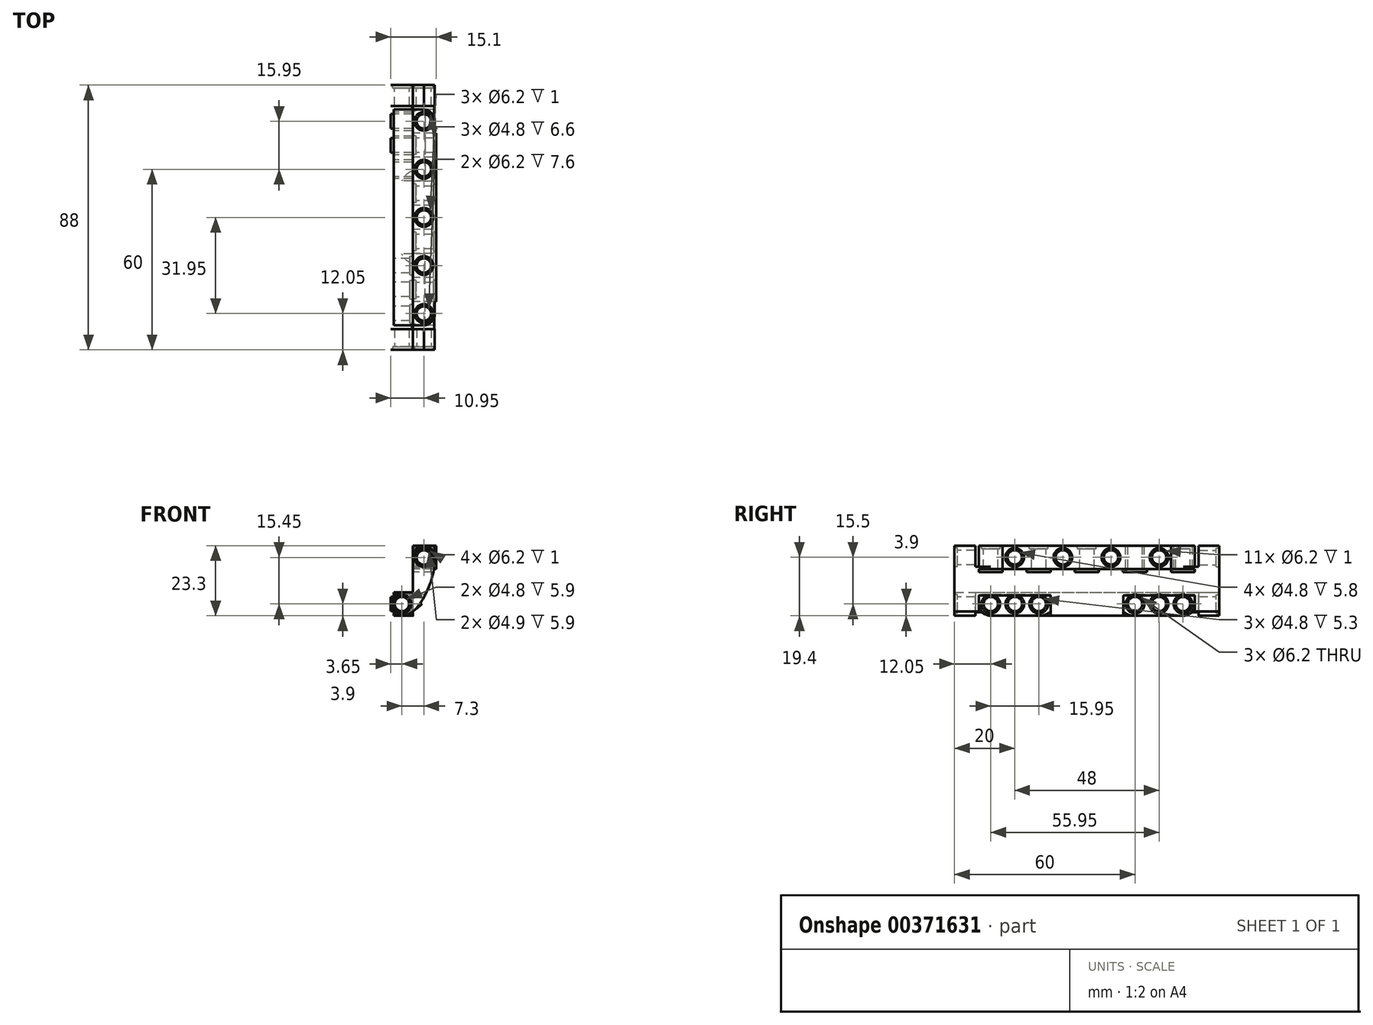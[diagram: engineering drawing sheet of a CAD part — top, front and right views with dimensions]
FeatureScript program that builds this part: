
annotation { "Feature Type Name" : "Feature", "Feature Type Description" : "" }
export const myFeature = defineFeature(function(context is Context, id is Id, definition is map)
    precondition{}
    {
        {
            var Q0;
            Q0=qCreatedBy(makeId("Front.planeOp"),FACE);
            var sketch = newSketch(context, id + "F0", { "sketchPlane" : qUnion([Q0])});
            skLineSegment(sketch, "E0", {"start": v(0, 0) * mm, "end": v(0, -11.65) * mm});
            skLineSegment(sketch, "E1", {"start": v(7.3, -11.65) * mm, "end": v(0, -11.65) * mm});
            skLineSegment(sketch, "E2", {"start": v(0, -11.65) * mm, "end": v(-7.3, -11.65) * mm});
            skLineSegment(sketch, "E3", {"start": v(-7.3, -11.65) * mm, "end": v(-7.3, -3.85) * mm});
            skLineSegment(sketch, "E4", {"start": v(-7.3, -3.85) * mm, "end": v(0, -3.85) * mm});
            skLineSegment(sketch, "E5", {"start": v(0, 0) * mm, "end": v(0, 11.65) * mm});
            skLineSegment(sketch, "E6", {"start": v(0, 11.65) * mm, "end": v(7.3, 11.65) * mm});
            skLineSegment(sketch, "E7", {"start": v(7.3, 11.65) * mm, "end": v(7.3, -11.65) * mm});
            skLineSegment(sketch, "E8", {"start": v(-3.65, -11.65) * mm, "end": v(-3.65, -3.85) * mm, "construction": true});
            skLineSegment(sketch, "E9", {"start": v(-7.3, -7.75) * mm, "end": v(0, -7.75) * mm, "construction": true});
            skLineSegment(sketch, "E10", {"start": v(3.65, 11.65) * mm, "end": v(3.65, -11.65) * mm, "construction": true});
            skLineSegment(sketch, "E11", {"start": v(7.3, 11.65) * mm, "end": v(7.3, 3.75) * mm, "construction": true});
            skLineSegment(sketch, "E12", {"start": v(7.3, 7.7) * mm, "end": v(0, 7.7) * mm, "construction": true});
            skLineSegment(sketch, "E13", {"start": v(0, -3.85) * mm, "end": v(4.5, -3.85) * mm, "construction": true});
            skFitSpline(sketch, "E14", {"points": [v(7.3, 7.7) * mm, v(4.5, -3.85) * mm, v(-3.65, -11.65) * mm], "startDerivative": vector(0, -23.4) * mm, "endDerivative": vector(-22.19, 0) * mm});
            skCircle(sketch, "E15", {"center": v(3.65, 7.7) * mm, "radius": 3.1 * mm});
            skCircle(sketch, "E16", {"center": v(3.65, 7.7) * mm, "radius": 2.45 * mm});
            skCircle(sketch, "E17", {"center": v(-3.65, -7.75) * mm, "radius": 2.45 * mm});
            skCircle(sketch, "E18", {"center": v(-3.65, -7.75) * mm, "radius": 3.1 * mm});
            skSolve(sketch);
        }
        {
            var Q0;
            {var subQ1=sQuery(id+"F0.wireOp",EDGE,"E5");Q0=makeQuery(id+"F0.imprint","IMPRINT",FACE,{"disambiguationData":[TD([[makeQuery(id+"F0.imprint","IMPRINT",EDGE,{"derivedFrom":subQ1}),-1.0]])]});}
            var Q1;
            {var subQ1=sQuery(id+"F0.wireOp",EDGE,"E3");Q1=makeQuery(id+"F0.imprint","IMPRINT",FACE,{"disambiguationData":[TD([[makeQuery(id+"F0.imprint","IMPRINT",EDGE,{"derivedFrom":subQ1}),-1.0]])]});}
            var Q2;
            Q2=makeQuery(id+"F0.imprint","IMPRINT",FACE,{"disambiguationData":[TD([[makeQuery(id+"F0.imprint","IMPRINT",EDGE,{"derivedFrom":sQuery(id+"F0.wireOp",EDGE,"E15")}),1.0]])]});
            var Q3;
            Q3=makeQuery(id+"F0.imprint","IMPRINT",FACE,{"disambiguationData":[TD([[makeQuery(id+"F0.imprint","IMPRINT",EDGE,{"derivedFrom":sQuery(id+"F0.wireOp",EDGE,"E16")}),1.0]])]});
            var Q4;
            Q4=makeQuery(id+"F0.imprint","IMPRINT",FACE,{"disambiguationData":[TD([[makeQuery(id+"F0.imprint","IMPRINT",EDGE,{"derivedFrom":sQuery(id+"F0.wireOp",EDGE,"E17")}),-1.0]])]});
            var Q5;
            Q5=makeQuery(id+"F0.imprint","IMPRINT",FACE,{"disambiguationData":[TD([[makeQuery(id+"F0.imprint","IMPRINT",EDGE,{"derivedFrom":sQuery(id+"F0.wireOp",EDGE,"E17")}),1.0]])]});
            extrude(context, id + "F1", {"entities" : qUnion([Q0, Q1, Q2, Q3, Q4, Q5]), "depth" : 88 * mm});
        }
        {
            var Q0;
            Q0=makeQuery(id+"F0.imprint","IMPRINT",FACE,{"disambiguationData":[TD([[makeQuery(id+"F0.imprint","IMPRINT",EDGE,{"derivedFrom":sQuery(id+"F0.wireOp",EDGE,"E17")}),1.0]])]});
            var Q1;
            Q1=makeQuery(id+"F0.imprint","IMPRINT",FACE,{"disambiguationData":[TD([[makeQuery(id+"F0.imprint","IMPRINT",EDGE,{"derivedFrom":sQuery(id+"F0.wireOp",EDGE,"E16")}),1.0]])]});
            extrude(context, id + "F2", {"entities" : qUnion([Q0, Q1]), "operationType" : NewBodyOperationType.REMOVE, "depth" : 7.8 * mm});
        }
        {
            var Q0;
            Q0=makeQuery(id+"F0.imprint","IMPRINT",FACE,{"disambiguationData":[TD([[makeQuery(id+"F0.imprint","IMPRINT",EDGE,{"derivedFrom":sQuery(id+"F0.wireOp",EDGE,"E17")}),-1.0]])]});
            var Q1;
            Q1=makeQuery(id+"F0.imprint","IMPRINT",FACE,{"disambiguationData":[TD([[makeQuery(id+"F0.imprint","IMPRINT",EDGE,{"derivedFrom":sQuery(id+"F0.wireOp",EDGE,"E15")}),1.0]])]});
            extrude(context, id + "F3", {"entities" : qUnion([Q0, Q1]), "operationType" : NewBodyOperationType.REMOVE, "depth" : 1 * mm});
        }
        {
            var Q0;
            Q0=makeQuery(id+"F1.opExtrude","SWEPT_FACE",FACE,{"disambiguationData":[OSD([sQuery(id+"F0.wireOp",EDGE,"E6")])]});
            var sketch = newSketch(context, id + "F4", { "sketchPlane" : qUnion([Q0])});
            skLineSegment(sketch, "E19", {"start": v(7.3, -44) * mm, "end": v(0, -44) * mm, "construction": true});
            skLineSegment(sketch, "E20", {"start": v(7.3, -44) * mm, "end": v(7.3, -76) * mm});
            skLineSegment(sketch, "E21", {"start": v(0, -44) * mm, "end": v(0, -48) * mm, "construction": true});
            skLineSegment(sketch, "E22", {"start": v(0, -48) * mm, "end": v(7.83, -48) * mm});
            skLineSegment(sketch, "E23", {"start": v(0, -48) * mm, "end": v(0, -56) * mm});
            skLineSegment(sketch, "E24", {"start": v(0, -56) * mm, "end": v(0, -64) * mm});
            skLineSegment(sketch, "E25", {"start": v(0, -64) * mm, "end": v(0, -72) * mm});
            skLineSegment(sketch, "E26", {"start": v(0, -72) * mm, "end": v(0, -76) * mm});
            skLineSegment(sketch, "E27", {"start": v(3.4, -79.9) * mm, "end": v(3.9, -79.9) * mm});
            skLineSegment(sketch, "E28", {"start": v(0, -72) * mm, "end": v(7.8, -72) * mm});
            skLineSegment(sketch, "E29", {"start": v(7.8, -72) * mm, "end": v(7.8, -44) * mm});
            skLineSegment(sketch, "E30", {"start": v(3.65, -79.9) * mm, "end": v(3.65, -44) * mm, "construction": true});
            skLineSegment(sketch, "E31", {"start": v(0, -60) * mm, "end": v(7.3, -60) * mm, "construction": true});
            skLineSegment(sketch, "E32", {"start": v(0, -75.95) * mm, "end": v(7.3, -75.95) * mm, "construction": true});
            skCircle(sketch, "E33", {"center": v(3.65, -75.95) * mm, "radius": 2.4 * mm});
            skCircle(sketch, "E34", {"center": v(3.65, -75.95) * mm, "radius": 3.1 * mm});
            skCircle(sketch, "E35", {"center": v(3.65, -60) * mm, "radius": 2.4 * mm});
            skCircle(sketch, "E36", {"center": v(3.65, -60) * mm, "radius": 3.1 * mm});
            skCircle(sketch, "E37", {"center": v(3.65, -44) * mm, "radius": 2.4 * mm});
            skCircle(sketch, "E38", {"center": v(3.65, -44) * mm, "radius": 3.1 * mm});
            skLineSegment(sketch, "E39.MirrorCS", {"start": v(7.8, -16) * mm, "end": v(7.8, -44) * mm});
            skLineSegment(sketch, "E40.MirrorCS", {"start": v(0, -16) * mm, "end": v(7.8, -16) * mm});
            skCircle(sketch, "E41.MirrorC", {"center": v(3.65, -12.05) * mm, "radius": 2.4 * mm});
            skCircle(sketch, "E42.MirrorC", {"center": v(3.65, -12.05) * mm, "radius": 3.1 * mm});
            skCircle(sketch, "E43.MirrorC", {"center": v(3.65, -28) * mm, "radius": 3.1 * mm});
            skCircle(sketch, "E44.MirrorC", {"center": v(3.65, -28) * mm, "radius": 2.4 * mm});
            skLineSegment(sketch, "E45.MirrorCS", {"start": v(0, -8.1) * mm, "end": v(7.3, -8.1) * mm});
            skLineSegment(sketch, "E46.MirrorCS", {"start": v(7.3, -44) * mm, "end": v(14.6, -44) * mm, "construction": true});
            skLineSegment(sketch, "E47.MirrorCS", {"start": v(7.3, -44) * mm, "end": v(7.3, -8.1) * mm});
            skLineSegment(sketch, "E48.MirrorCS", {"start": v(0, -16) * mm, "end": v(0, -8.1) * mm});
            skPoint(sketch, "E49.visualSharp", {"position": v(7.3, -79.9) * mm});
            skArc(sketch, "E49.filletArc", {"start": v(3.4, -79.9) * mm, "mid": v(6.16, -78.76) * mm, "end": v(7.3, -76) * mm});
            skPoint(sketch, "E50.visualSharp", {"position": v(0, -79.9) * mm});
            skArc(sketch, "E50.filletArc", {"start": v(0, -76) * mm, "mid": v(1.14, -78.76) * mm, "end": v(3.9, -79.9) * mm});
            skArc(sketch, "E51.MirrorCS", {"start": v(3.4, -8.1) * mm, "mid": v(6.16, -9.24) * mm, "end": v(7.3, -12) * mm});
            skArc(sketch, "E52.MirrorCS", {"start": v(0, -12) * mm, "mid": v(1.14, -9.24) * mm, "end": v(3.9, -8.1) * mm});
            skLineSegment(sketch, "E53", {"start": v(7.3, -88) * mm, "end": v(7.3, -81.1) * mm});
            skLineSegment(sketch, "E54", {"start": v(7.3, -81.1) * mm, "end": v(0, -81.1) * mm});
            skLineSegment(sketch, "E55", {"start": v(0, -81.1) * mm, "end": v(0, -79.9) * mm});
            skLineSegment(sketch, "E56", {"start": v(7.3, -79.9) * mm, "end": v(0, -79.9) * mm});
            skLineSegment(sketch, "E57.MirrorCS", {"start": v(7.3, -8.1) * mm, "end": v(0, -8.1) * mm});
            skLineSegment(sketch, "E58.MirrorCS", {"start": v(7.3, -6.9) * mm, "end": v(0, -6.9) * mm});
            skSolve(sketch);
        }
        {
            var Q0;
            {var subQ0=sQuery(id+"F4.wireOp",EDGE,"E58.MirrorCS");Q0=makeQuery(id+"F4.imprint","IMPRINT",FACE,{"disambiguationData":[TD([[makeQuery(id+"F4.imprint","IMPRINT",EDGE,{"derivedFrom":subQ0}),1.0]])]});}
            var Q1;
            {var subQ7=sQuery(id+"F4.wireOp",EDGE,"E54");Q1=makeQuery(id+"F4.imprint","IMPRINT",FACE,{"disambiguationData":[TD([[makeQuery(id+"F4.imprint","IMPRINT",EDGE,{"derivedFrom":subQ7}),-1.0]])]});}
            extrude(context, id + "F5", {"entities" : qUnion([Q0, Q1]), "operationType" : NewBodyOperationType.REMOVE, "oppositeDirection" : true, "depth" : 7 * mm});
        }
        {
            var Q0;
            Q0=makeQuery(id+"F4.imprint","IMPRINT",FACE,{"disambiguationData":[TD([[makeQuery(id+"F4.imprint","IMPRINT",EDGE,{"derivedFrom":sQuery(id+"F4.wireOp",EDGE,"E41.MirrorC")}),-1.0]])]});
            var Q1;
            Q1=makeQuery(id+"F4.imprint","IMPRINT",FACE,{"disambiguationData":[TD([[makeQuery(id+"F4.imprint","IMPRINT",EDGE,{"derivedFrom":sQuery(id+"F4.wireOp",EDGE,"E44.MirrorC")}),-1.0]])]});
            var Q2;
            Q2=makeQuery(id+"F4.imprint","IMPRINT",FACE,{"disambiguationData":[TD([[makeQuery(id+"F4.imprint","IMPRINT",EDGE,{"derivedFrom":sQuery(id+"F4.wireOp",EDGE,"E37")}),1.0]])]});
            var Q3;
            Q3=makeQuery(id+"F4.imprint","IMPRINT",FACE,{"disambiguationData":[TD([[makeQuery(id+"F4.imprint","IMPRINT",EDGE,{"derivedFrom":sQuery(id+"F4.wireOp",EDGE,"E35")}),1.0]])]});
            var Q4;
            Q4=makeQuery(id+"F4.imprint","IMPRINT",FACE,{"disambiguationData":[TD([[makeQuery(id+"F4.imprint","IMPRINT",EDGE,{"derivedFrom":sQuery(id+"F4.wireOp",EDGE,"E33")}),1.0]])]});
            extrude(context, id + "F6", {"entities" : qUnion([Q0, Q1, Q2, Q3, Q4]), "operationType" : NewBodyOperationType.REMOVE, "oppositeDirection" : true, "depth" : 7.6 * mm});
        }
        {
            var Q0;
            Q0=makeQuery(id+"F4.imprint","IMPRINT",FACE,{"disambiguationData":[TD([[makeQuery(id+"F4.imprint","IMPRINT",EDGE,{"derivedFrom":sQuery(id+"F4.wireOp",EDGE,"E41.MirrorC")}),1.0]])]});
            var Q1;
            Q1=makeQuery(id+"F4.imprint","IMPRINT",FACE,{"disambiguationData":[TD([[makeQuery(id+"F4.imprint","IMPRINT",EDGE,{"derivedFrom":sQuery(id+"F4.wireOp",EDGE,"E43.MirrorC")}),-1.0]])]});
            var Q2;
            Q2=makeQuery(id+"F4.imprint","IMPRINT",FACE,{"disambiguationData":[TD([[makeQuery(id+"F4.imprint","IMPRINT",EDGE,{"derivedFrom":sQuery(id+"F4.wireOp",EDGE,"E37")}),-1.0]])]});
            var Q3;
            Q3=makeQuery(id+"F4.imprint","IMPRINT",FACE,{"disambiguationData":[TD([[makeQuery(id+"F4.imprint","IMPRINT",EDGE,{"derivedFrom":sQuery(id+"F4.wireOp",EDGE,"E35")}),-1.0]])]});
            var Q4;
            Q4=makeQuery(id+"F4.imprint","IMPRINT",FACE,{"disambiguationData":[TD([[makeQuery(id+"F4.imprint","IMPRINT",EDGE,{"derivedFrom":sQuery(id+"F4.wireOp",EDGE,"E33")}),-1.0]])]});
            extrude(context, id + "F7", {"entities" : qUnion([Q0, Q1, Q2, Q3, Q4]), "operationType" : NewBodyOperationType.REMOVE, "oppositeDirection" : true, "depth" : 1 * mm});
        }
        {
            var Q0;
            Q0=makeQuery(id+"F1.opExtrude","CAP_FACE",FACE,{"disambiguationData":[OSD([sQuery(id+"F0.wireOp",EDGE,"E0"),sQuery(id+"F0.wireOp",EDGE,"E2"),sQuery(id+"F0.wireOp",EDGE,"E3"),sQuery(id+"F0.wireOp",EDGE,"E4"),sQuery(id+"F0.wireOp",EDGE,"E5"),sQuery(id+"F0.wireOp",EDGE,"E6"),sQuery(id+"F0.wireOp",EDGE,"E7"),sQuery(id+"F0.wireOp",EDGE,"E14")])],"isStart":false});
            var sketch = newSketch(context, id + "F8", { "sketchPlane" : qUnion([Q0])});
            skLineSegment(sketch, "E59", {"start": v(3.65, 11.65) * mm, "end": v(3.65, 4.4) * mm, "construction": true});
            skPoint(sketch, "E59.endSnap0", {"position": v(3.65, 11.65) * mm});
            skLineSegment(sketch, "E60", {"start": v(7.3, 7.7) * mm, "end": v(0, 7.7) * mm, "construction": true});
            skCircle(sketch, "E61", {"center": v(3.65, 7.7) * mm, "radius": 2.4 * mm});
            skCircle(sketch, "E62", {"center": v(3.65, 7.7) * mm, "radius": 3.1 * mm});
            skLineSegment(sketch, "E63", {"start": v(-3.65, -11.65) * mm, "end": v(-3.65, -3.85) * mm, "construction": true});
            skLineSegment(sketch, "E64", {"start": v(-7.3, -7.75) * mm, "end": v(0, -7.75) * mm, "construction": true});
            skCircle(sketch, "E65", {"center": v(-3.65, -7.75) * mm, "radius": 2.4 * mm});
            skCircle(sketch, "E66", {"center": v(-3.65, -7.75) * mm, "radius": 3.1 * mm});
            skSolve(sketch);
        }
        {
            var Q0;
            Q0=makeQuery(id+"F8.imprint","IMPRINT",FACE,{"disambiguationData":[TD([[makeQuery(id+"F8.imprint","IMPRINT",EDGE,{"derivedFrom":sQuery(id+"F8.wireOp",EDGE,"E61")}),1.0]])]});
            var Q1;
            Q1=makeQuery(id+"F8.imprint","IMPRINT",FACE,{"disambiguationData":[TD([[makeQuery(id+"F8.imprint","IMPRINT",EDGE,{"derivedFrom":sQuery(id+"F8.wireOp",EDGE,"E65")}),1.0]])]});
            extrude(context, id + "F9", {"entities" : qUnion([Q0, Q1]), "operationType" : NewBodyOperationType.REMOVE, "oppositeDirection" : true, "depth" : 7.8 * mm});
        }
        {
            var Q0;
            Q0=makeQuery(id+"F8.imprint","IMPRINT",FACE,{"disambiguationData":[TD([[makeQuery(id+"F8.imprint","IMPRINT",EDGE,{"derivedFrom":sQuery(id+"F8.wireOp",EDGE,"E61")}),-1.0]])]});
            var Q1;
            Q1=makeQuery(id+"F8.imprint","IMPRINT",FACE,{"disambiguationData":[TD([[makeQuery(id+"F8.imprint","IMPRINT",EDGE,{"derivedFrom":sQuery(id+"F8.wireOp",EDGE,"E65")}),-1.0]])]});
            extrude(context, id + "F10", {"entities" : qUnion([Q0, Q1]), "operationType" : NewBodyOperationType.REMOVE, "oppositeDirection" : true, "depth" : 1 * mm});
        }
        {
            var Q0;
            {var subQ0=sQuery(id+"F4.wireOp",EDGE,"E28");var subQ1=sQuery(id+"F4.wireOp",EDGE,"E20");var subQ2=makeQuery(id+"F4.imprint","INTERSECT",VERTEX,{"derivedFrom":[subQ1,subQ0]});Q0=makeQuery(id+"F4.imprint","IMPRINT",FACE,{"disambiguationData":[TD([[makeQuery(id+"F4.imprint","IMPRINT",EDGE,{"disambiguationData":[TD([[subQ2,-1.0]])],"derivedFrom":subQ1}),-1.0]])]});}
            var Q1;
            {var subQ0=sQuery(id+"F4.wireOp",EDGE,"E39.MirrorCS");Q1=makeQuery(id+"F4.imprint","IMPRINT",FACE,{"disambiguationData":[TD([[makeQuery(id+"F4.imprint","IMPRINT",EDGE,{"derivedFrom":subQ0}),-1.0]])]});}
            var Q2;
            {var subQ0=sQuery(id+"F4.wireOp",EDGE,"E23");Q2=makeQuery(id+"F4.imprint","IMPRINT",FACE,{"disambiguationData":[TD([[makeQuery(id+"F4.imprint","IMPRINT",EDGE,{"derivedFrom":subQ0}),-1.0]])]});}
            var Q3;
            Q3=makeQuery(id+"F4.imprint","IMPRINT",FACE,{"disambiguationData":[TD([[makeQuery(id+"F4.imprint","IMPRINT",EDGE,{"derivedFrom":sQuery(id+"F4.wireOp",EDGE,"E38")}),-1.0]])]});
            extrude(context, id + "F11", {"entities" : qUnion([Q0, Q1, Q2, Q3]), "operationType" : NewBodyOperationType.ADD, "oppositeDirection" : true, "depth" : 7.8 * mm});
        }
        {
            var Q0;
            Q0=makeQuery(id+"F1.opExtrude","SWEPT_FACE",FACE,{"disambiguationData":[OSD([sQuery(id+"F0.wireOp",EDGE,"E0"),sQuery(id+"F0.wireOp",EDGE,"E5")])]});
            var sketch = newSketch(context, id + "F12", { "sketchPlane" : qUnion([Q0])});
            skLineSegment(sketch, "E67", {"start": v(8.1, 11.65) * mm, "end": v(16, 11.65) * mm, "construction": true});
            skLineSegment(sketch, "E68", {"start": v(16, 11.65) * mm, "end": v(16, 3.85) * mm, "construction": true});
            skLineSegment(sketch, "E69", {"start": v(16, 3.85) * mm, "end": v(24, 3.85) * mm});
            skLineSegment(sketch, "E70", {"start": v(24, 3.85) * mm, "end": v(32, 3.85) * mm});
            skLineSegment(sketch, "E71", {"start": v(32, 3.85) * mm, "end": v(40, 3.85) * mm});
            skLineSegment(sketch, "E72", {"start": v(40, 3.85) * mm, "end": v(48, 3.85) * mm});
            skLineSegment(sketch, "E73", {"start": v(24, 3.85) * mm, "end": v(24, 11.65) * mm, "construction": true});
            skLineSegment(sketch, "E74", {"start": v(20, 3.85) * mm, "end": v(20, 11.65) * mm, "construction": true});
            skLineSegment(sketch, "E75", {"start": v(24, 7.75) * mm, "end": v(16, 7.75) * mm, "construction": true});
            skLineSegment(sketch, "E76", {"start": v(32, 3.85) * mm, "end": v(32, 11.65) * mm, "construction": true});
            skLineSegment(sketch, "E77", {"start": v(40, 3.85) * mm, "end": v(40, 11.65) * mm, "construction": true});
            skLineSegment(sketch, "E78", {"start": v(40, 7.75) * mm, "end": v(32, 7.75) * mm, "construction": true});
            skLineSegment(sketch, "E79", {"start": v(36, 3.85) * mm, "end": v(36, 11.65) * mm, "construction": true});
            skLineSegment(sketch, "E80", {"start": v(48, 3.85) * mm, "end": v(56, 3.85) * mm});
            skLineSegment(sketch, "E81", {"start": v(56, 3.85) * mm, "end": v(64, 3.85) * mm});
            skLineSegment(sketch, "E82", {"start": v(64, 3.85) * mm, "end": v(72, 3.85) * mm});
            skLineSegment(sketch, "E83", {"start": v(72, 3.85) * mm, "end": v(79.9, 3.85) * mm});
            skLineSegment(sketch, "E84", {"start": v(16, 3.85) * mm, "end": v(8.1, 3.85) * mm});
            skLineSegment(sketch, "E85", {"start": v(48, 3.85) * mm, "end": v(48, 11.65) * mm, "construction": true});
            skLineSegment(sketch, "E86", {"start": v(56, 3.85) * mm, "end": v(56, 11.65) * mm, "construction": true});
            skLineSegment(sketch, "E87", {"start": v(72, 3.85) * mm, "end": v(72, 11.65) * mm, "construction": true});
            skLineSegment(sketch, "E88", {"start": v(64, 3.85) * mm, "end": v(64, 11.65) * mm, "construction": true});
            skLineSegment(sketch, "E89", {"start": v(72, 7.75) * mm, "end": v(64, 7.75) * mm, "construction": true});
            skLineSegment(sketch, "E90", {"start": v(68, 3.85) * mm, "end": v(68, 11.65) * mm, "construction": true});
            skPoint(sketch, "E90.endSnap0", {"position": v(68, 7.75) * mm});
            skLineSegment(sketch, "E91", {"start": v(56, 7.75) * mm, "end": v(48, 7.75) * mm, "construction": true});
            skLineSegment(sketch, "E92", {"start": v(52, 3.85) * mm, "end": v(52, 11.65) * mm, "construction": true});
            skCircle(sketch, "E93", {"center": v(20, 7.75) * mm, "radius": 2.4 * mm});
            skCircle(sketch, "E94", {"center": v(20, 7.75) * mm, "radius": 3.1 * mm});
            skCircle(sketch, "E95", {"center": v(36, 7.75) * mm, "radius": 2.4 * mm});
            skCircle(sketch, "E96", {"center": v(36, 7.75) * mm, "radius": 3.1 * mm});
            skCircle(sketch, "E97", {"center": v(52, 7.75) * mm, "radius": 2.4 * mm});
            skCircle(sketch, "E98", {"center": v(52, 7.75) * mm, "radius": 3.1 * mm});
            skCircle(sketch, "E99", {"center": v(68, 7.75) * mm, "radius": 2.4 * mm});
            skCircle(sketch, "E100", {"center": v(68, 7.75) * mm, "radius": 3.1 * mm});
            skLineSegment(sketch, "E101", {"start": v(8.1, 3.85) * mm, "end": v(8.1, 2.85) * mm});
            skLineSegment(sketch, "E102", {"start": v(8.1, 2.85) * mm, "end": v(79.9, 2.85) * mm});
            skLineSegment(sketch, "E103", {"start": v(79.9, 2.85) * mm, "end": v(79.9, 3.85) * mm});
            skLineSegment(sketch, "E104", {"start": v(16, 3.85) * mm, "end": v(16, 2.85) * mm});
            skLineSegment(sketch, "E105", {"start": v(24, 3.85) * mm, "end": v(24, 2.85) * mm});
            skLineSegment(sketch, "E106", {"start": v(32, 3.85) * mm, "end": v(32, 2.85) * mm});
            skLineSegment(sketch, "E107", {"start": v(40, 3.85) * mm, "end": v(40, 2.85) * mm});
            skLineSegment(sketch, "E108", {"start": v(48, 3.85) * mm, "end": v(48, 2.85) * mm});
            skLineSegment(sketch, "E109", {"start": v(56, 3.85) * mm, "end": v(56, 2.85) * mm});
            skLineSegment(sketch, "E110", {"start": v(64, 3.85) * mm, "end": v(64, 2.85) * mm});
            skLineSegment(sketch, "E111", {"start": v(72, 3.85) * mm, "end": v(72, 2.85) * mm});
            skSolve(sketch);
        }
        {
            var Q0;
            Q0=makeQuery(id+"F12.imprint","IMPRINT",FACE,{"disambiguationData":[TD([[makeQuery(id+"F12.imprint","IMPRINT",EDGE,{"derivedFrom":sQuery(id+"F12.wireOp",EDGE,"E93")}),1.0]])]});
            var Q1;
            Q1=makeQuery(id+"F12.imprint","IMPRINT",FACE,{"disambiguationData":[TD([[makeQuery(id+"F12.imprint","IMPRINT",EDGE,{"derivedFrom":sQuery(id+"F12.wireOp",EDGE,"E95")}),1.0]])]});
            var Q2;
            Q2=makeQuery(id+"F12.imprint","IMPRINT",FACE,{"disambiguationData":[TD([[makeQuery(id+"F12.imprint","IMPRINT",EDGE,{"derivedFrom":sQuery(id+"F12.wireOp",EDGE,"E97")}),1.0]])]});
            var Q3;
            Q3=makeQuery(id+"F12.imprint","IMPRINT",FACE,{"disambiguationData":[TD([[makeQuery(id+"F12.imprint","IMPRINT",EDGE,{"derivedFrom":sQuery(id+"F12.wireOp",EDGE,"E99")}),1.0]])]});
            extrude(context, id + "F13", {"entities" : qUnion([Q0, Q1, Q2, Q3]), "operationType" : NewBodyOperationType.REMOVE, "oppositeDirection" : true, "depth" : 25 * mm});
        }
        {
            var Q0;
            Q0=makeQuery(id+"F12.imprint","IMPRINT",FACE,{"disambiguationData":[TD([[makeQuery(id+"F12.imprint","IMPRINT",EDGE,{"derivedFrom":sQuery(id+"F12.wireOp",EDGE,"E93")}),-1.0]])]});
            var Q1;
            Q1=makeQuery(id+"F12.imprint","IMPRINT",FACE,{"disambiguationData":[TD([[makeQuery(id+"F12.imprint","IMPRINT",EDGE,{"derivedFrom":sQuery(id+"F12.wireOp",EDGE,"E95")}),-1.0]])]});
            var Q2;
            Q2=makeQuery(id+"F12.imprint","IMPRINT",FACE,{"disambiguationData":[TD([[makeQuery(id+"F12.imprint","IMPRINT",EDGE,{"derivedFrom":sQuery(id+"F12.wireOp",EDGE,"E97")}),-1.0]])]});
            var Q3;
            Q3=makeQuery(id+"F12.imprint","IMPRINT",FACE,{"disambiguationData":[TD([[makeQuery(id+"F12.imprint","IMPRINT",EDGE,{"derivedFrom":sQuery(id+"F12.wireOp",EDGE,"E99")}),-1.0]])]});
            extrude(context, id + "F14", {"entities" : qUnion([Q0, Q1, Q2, Q3]), "operationType" : NewBodyOperationType.REMOVE, "oppositeDirection" : true, "depth" : 1 * mm});
        }
        {
            var Q0;
            Q0=makeQuery(id+"F12.imprint","IMPRINT",FACE,{"disambiguationData":[TD([[makeQuery(id+"F12.imprint","IMPRINT",EDGE,{"derivedFrom":sQuery(id+"F12.wireOp",EDGE,"E84")}),1.0]])]});
            var Q1;
            Q1=makeQuery(id+"F12.imprint","IMPRINT",FACE,{"disambiguationData":[TD([[makeQuery(id+"F12.imprint","IMPRINT",EDGE,{"derivedFrom":sQuery(id+"F12.wireOp",EDGE,"E70")}),-1.0]])]});
            var Q2;
            Q2=makeQuery(id+"F12.imprint","IMPRINT",FACE,{"disambiguationData":[TD([[makeQuery(id+"F12.imprint","IMPRINT",EDGE,{"derivedFrom":sQuery(id+"F12.wireOp",EDGE,"E72")}),-1.0]])]});
            var Q3;
            Q3=makeQuery(id+"F12.imprint","IMPRINT",FACE,{"disambiguationData":[TD([[makeQuery(id+"F12.imprint","IMPRINT",EDGE,{"derivedFrom":sQuery(id+"F12.wireOp",EDGE,"E81")}),-1.0]])]});
            var Q4;
            Q4=makeQuery(id+"F12.imprint","IMPRINT",FACE,{"disambiguationData":[TD([[makeQuery(id+"F12.imprint","IMPRINT",EDGE,{"derivedFrom":sQuery(id+"F12.wireOp",EDGE,"E83")}),-1.0]])]});
            extrude(context, id + "F15", {"entities" : qUnion([Q0, Q1, Q2, Q3, Q4]), "operationType" : NewBodyOperationType.REMOVE, "oppositeDirection" : true, "depth" : 7 * mm});
        }
        {
            var Q0;
            Q0=makeQuery(id+"F11.opExtrude","SWEPT_FACE",FACE,{"disambiguationData":[OSD([sQuery(id+"F4.wireOp",EDGE,"E29"),sQuery(id+"F4.wireOp",EDGE,"E39.MirrorCS")])]});
            var sketch = newSketch(context, id + "F16", { "sketchPlane" : qUnion([Q0])});
            skCircle(sketch, "E112", {"center": v(-68, 7.75) * mm, "radius": 3.1 * mm});
            skCircle(sketch, "E113", {"center": v(-52, 7.75) * mm, "radius": 3.1 * mm});
            skCircle(sketch, "E114", {"center": v(-36, 7.75) * mm, "radius": 3.1 * mm});
            skCircle(sketch, "E115", {"center": v(-20, 7.75) * mm, "radius": 3.1 * mm});
            skSolve(sketch);
        }
        {
            var Q0;
            Q0=makeQuery(id+"F16.imprint","IMPRINT",FACE,{"disambiguationData":[TD([[makeQuery(id+"F16.imprint","IMPRINT",EDGE,{"derivedFrom":sQuery(id+"F16.wireOp",EDGE,"E112")}),1.0]])]});
            var Q1;
            Q1=makeQuery(id+"F16.imprint","IMPRINT",FACE,{"disambiguationData":[TD([[makeQuery(id+"F16.imprint","IMPRINT",EDGE,{"derivedFrom":sQuery(id+"F16.wireOp",EDGE,"E113")}),1.0]])]});
            var Q2;
            Q2=makeQuery(id+"F16.imprint","IMPRINT",FACE,{"disambiguationData":[TD([[makeQuery(id+"F16.imprint","IMPRINT",EDGE,{"derivedFrom":sQuery(id+"F16.wireOp",EDGE,"E114")}),1.0]])]});
            var Q3;
            Q3=makeQuery(id+"F16.imprint","IMPRINT",FACE,{"disambiguationData":[TD([[makeQuery(id+"F16.imprint","IMPRINT",EDGE,{"derivedFrom":sQuery(id+"F16.wireOp",EDGE,"E115")}),1.0]])]});
            extrude(context, id + "F17", {"entities" : qUnion([Q0, Q1, Q2, Q3]), "operationType" : NewBodyOperationType.REMOVE, "oppositeDirection" : true, "depth" : 1 * mm});
        }
        {
            var Q0;
            Q0=makeQuery(id+"F1.opExtrude","SWEPT_FACE",FACE,{"disambiguationData":[OSD([sQuery(id+"F0.wireOp",EDGE,"E3")])]});
            var sketch = newSketch(context, id + "F18", { "sketchPlane" : qUnion([Q0])});
            skLineSegment(sketch, "E116", {"start": v(44, -11.65) * mm, "end": v(44, -3.85) * mm, "construction": true});
            skLineSegment(sketch, "E117", {"start": v(88, -11.65) * mm, "end": v(79.9, -11.65) * mm, "construction": true});
            skLineSegment(sketch, "E118", {"start": v(79.9, -11.65) * mm, "end": v(79.9, -3.85) * mm});
            skLineSegment(sketch, "E119", {"start": v(79.9, -3.85) * mm, "end": v(81.1, -3.85) * mm});
            skLineSegment(sketch, "E120", {"start": v(81.1, -3.85) * mm, "end": v(81.1, -11.65) * mm});
            skLineSegment(sketch, "E121", {"start": v(79.9, -11.65) * mm, "end": v(72, -11.65) * mm});
            skLineSegment(sketch, "E122", {"start": v(72, -11.65) * mm, "end": v(64, -11.65) * mm});
            skLineSegment(sketch, "E123", {"start": v(64, -11.65) * mm, "end": v(56, -11.65) * mm});
            skLineSegment(sketch, "E124", {"start": v(56, -11.65) * mm, "end": v(56, -3.85) * mm, "construction": true});
            skLineSegment(sketch, "E125", {"start": v(60, -11.65) * mm, "end": v(60, -3.85) * mm, "construction": true});
            skLineSegment(sketch, "E126", {"start": v(68, -11.65) * mm, "end": v(68, -3.85) * mm, "construction": true});
            skLineSegment(sketch, "E127", {"start": v(75.95, -11.65) * mm, "end": v(75.95, -3.85) * mm, "construction": true});
            skLineSegment(sketch, "E128", {"start": v(79.9, -7.75) * mm, "end": v(56, -7.75) * mm, "construction": true});
            skCircle(sketch, "E129", {"center": v(75.95, -7.75) * mm, "radius": 2.4 * mm});
            skCircle(sketch, "E130", {"center": v(75.95, -7.75) * mm, "radius": 3.1 * mm});
            skCircle(sketch, "E131", {"center": v(67.95, -7.75) * mm, "radius": 2.4 * mm});
            skCircle(sketch, "E132", {"center": v(67.95, -7.75) * mm, "radius": 3.1 * mm});
            skCircle(sketch, "E133", {"center": v(60, -7.75) * mm, "radius": 2.4 * mm});
            skCircle(sketch, "E134", {"center": v(60, -7.75) * mm, "radius": 3.1 * mm});
            skCircle(sketch, "E135.MirrorC", {"center": v(28, -7.75) * mm, "radius": 2.4 * mm});
            skCircle(sketch, "E136.MirrorC", {"center": v(28, -7.75) * mm, "radius": 3.1 * mm});
            skCircle(sketch, "E137.MirrorC", {"center": v(20.05, -7.75) * mm, "radius": 3.1 * mm});
            skCircle(sketch, "E138.MirrorC", {"center": v(20.05, -7.75) * mm, "radius": 2.4 * mm});
            skCircle(sketch, "E139.MirrorC", {"center": v(12.05, -7.75) * mm, "radius": 3.1 * mm});
            skCircle(sketch, "E140.MirrorC", {"center": v(12.05, -7.75) * mm, "radius": 2.4 * mm});
            skLineSegment(sketch, "E141.MirrorCS", {"start": v(8.1, -11.65) * mm, "end": v(8.1, -3.85) * mm});
            skLineSegment(sketch, "E142.MirrorCS", {"start": v(32, -11.65) * mm, "end": v(32, -3.85) * mm, "construction": true});
            skLineSegment(sketch, "E143.MirrorCS", {"start": v(6.9, -3.85) * mm, "end": v(6.9, -11.65) * mm});
            skSolve(sketch);
        }
        {
            var Q0;
            Q0=makeQuery(id+"F18.imprint","IMPRINT",FACE,{"disambiguationData":[TD([[makeQuery(id+"F18.imprint","IMPRINT",EDGE,{"derivedFrom":sQuery(id+"F18.wireOp",EDGE,"E129")}),-1.0]])]});
            var Q1;
            Q1=makeQuery(id+"F18.imprint","IMPRINT",FACE,{"disambiguationData":[TD([[makeQuery(id+"F18.imprint","IMPRINT",EDGE,{"derivedFrom":sQuery(id+"F18.wireOp",EDGE,"E131")}),-1.0]])]});
            var Q2;
            Q2=makeQuery(id+"F18.imprint","IMPRINT",FACE,{"disambiguationData":[TD([[makeQuery(id+"F18.imprint","IMPRINT",EDGE,{"derivedFrom":sQuery(id+"F18.wireOp",EDGE,"E133")}),-1.0]])]});
            var Q3;
            Q3=makeQuery(id+"F18.imprint","IMPRINT",FACE,{"disambiguationData":[TD([[makeQuery(id+"F18.imprint","IMPRINT",EDGE,{"derivedFrom":sQuery(id+"F18.wireOp",EDGE,"E135.MirrorC")}),1.0]])]});
            var Q4;
            Q4=makeQuery(id+"F18.imprint","IMPRINT",FACE,{"disambiguationData":[TD([[makeQuery(id+"F18.imprint","IMPRINT",EDGE,{"derivedFrom":sQuery(id+"F18.wireOp",EDGE,"E137.MirrorC")}),-1.0]])]});
            var Q5;
            Q5=makeQuery(id+"F18.imprint","IMPRINT",FACE,{"disambiguationData":[TD([[makeQuery(id+"F18.imprint","IMPRINT",EDGE,{"derivedFrom":sQuery(id+"F18.wireOp",EDGE,"E139.MirrorC")}),-1.0]])]});
            extrude(context, id + "F19", {"entities" : qUnion([Q0, Q1, Q2, Q3, Q4, Q5]), "operationType" : NewBodyOperationType.REMOVE, "oppositeDirection" : true, "depth" : 1 * mm});
        }
        {
            var Q0;
            Q0=makeQuery(id+"F1.opExtrude","SWEPT_FACE",FACE,{"disambiguationData":[OSD([sQuery(id+"F0.wireOp",EDGE,"E2")])]});
            var sketch = newSketch(context, id + "F20", { "sketchPlane" : qUnion([Q0])});
            skLineSegment(sketch, "E144", {"start": v(-7.3, 88) * mm, "end": v(-7.3, 79.9) * mm});
            skLineSegment(sketch, "E145", {"start": v(-7.3, 79.9) * mm, "end": v(0, 79.9) * mm});
            skLineSegment(sketch, "E146", {"start": v(0, 79.9) * mm, "end": v(4, 79.9) * mm});
            skLineSegment(sketch, "E147", {"start": v(4, 79.9) * mm, "end": v(4, 56.1) * mm});
            skLineSegment(sketch, "E148", {"start": v(4, 56.1) * mm, "end": v(0, 56.1) * mm});
            skLineSegment(sketch, "E149", {"start": v(0, 56.1) * mm, "end": v(0, 79.9) * mm});
            skLineSegment(sketch, "E150", {"start": v(0, 56.1) * mm, "end": v(-7.3, 56.1) * mm});
            skLineSegment(sketch, "E151", {"start": v(-7.3, 44) * mm, "end": v(-0.96, 44) * mm, "construction": true});
            skPoint(sketch, "E151.endSnap0", {"position": v(-3.65, 44) * mm});
            skLineSegment(sketch, "E152.MirrorCS", {"start": v(0, 31.9) * mm, "end": v(-7.3, 31.9) * mm});
            skLineSegment(sketch, "E153.MirrorCS", {"start": v(0, 31.9) * mm, "end": v(0, 8.1) * mm});
            skLineSegment(sketch, "E154.MirrorCS", {"start": v(4, 31.9) * mm, "end": v(0, 31.9) * mm});
            skLineSegment(sketch, "E155.MirrorCS", {"start": v(4, 8.1) * mm, "end": v(4, 31.9) * mm});
            skLineSegment(sketch, "E156.MirrorCS", {"start": v(-7.3, 8.1) * mm, "end": v(0, 8.1) * mm});
            skLineSegment(sketch, "E157.MirrorCS", {"start": v(0, 8.1) * mm, "end": v(4, 8.1) * mm});
            skSolve(sketch);
        }
        {
            var Q0;
            Q0=makeQuery(id+"F20.imprint","IMPRINT",FACE,{"disambiguationData":[TD([[makeQuery(id+"F20.imprint","IMPRINT",EDGE,{"derivedFrom":sQuery(id+"F20.wireOp",EDGE,"E153.MirrorCS")}),1.0]])]});
            var Q1;
            Q1=makeQuery(id+"F20.imprint","IMPRINT",FACE,{"disambiguationData":[TD([[makeQuery(id+"F20.imprint","IMPRINT",EDGE,{"derivedFrom":sQuery(id+"F20.wireOp",EDGE,"E146")}),-1.0]])]});
            var Q2;
            {var subQ0=sQuery(id+"F20.wireOp",EDGE,"E149");Q2=makeQuery(id+"F20.imprint","IMPRINT",FACE,{"disambiguationData":[TD([[makeQuery(id+"F20.imprint","IMPRINT",EDGE,{"derivedFrom":subQ0}),1.0]])]});}
            var Q3;
            {var subQ0=sQuery(id+"F20.wireOp",EDGE,"E153.MirrorCS");Q3=makeQuery(id+"F20.imprint","IMPRINT",FACE,{"disambiguationData":[TD([[makeQuery(id+"F20.imprint","IMPRINT",EDGE,{"derivedFrom":subQ0}),-1.0]])]});}
            extrude(context, id + "F21", {"entities" : qUnion([Q0, Q1, Q2, Q3]), "operationType" : NewBodyOperationType.ADD, "oppositeDirection" : true, "depth" : 7.8 * mm});
        }
        {
            var Q0;
            Q0=makeQuery(id+"F20.imprint","IMPRINT",FACE,{"disambiguationData":[TD([[makeQuery(id+"F20.imprint","IMPRINT",EDGE,{"derivedFrom":sQuery(id+"F20.wireOp",EDGE,"E146")}),-1.0]])]});
            var Q1;
            Q1=makeQuery(id+"F20.imprint","IMPRINT",FACE,{"disambiguationData":[TD([[makeQuery(id+"F20.imprint","IMPRINT",EDGE,{"derivedFrom":sQuery(id+"F20.wireOp",EDGE,"E153.MirrorCS")}),1.0]])]});
            extrude(context, id + "F22", {"entities" : qUnion([Q0, Q1]), "operationType" : NewBodyOperationType.REMOVE, "oppositeDirection" : true, "depth" : 7 * mm});
        }
        {
            var Q0;
            Q0=makeQuery(id+"F18.imprint","IMPRINT",FACE,{"disambiguationData":[TD([[makeQuery(id+"F18.imprint","IMPRINT",EDGE,{"derivedFrom":sQuery(id+"F18.wireOp",EDGE,"E129")}),1.0]])]});
            var Q1;
            Q1=makeQuery(id+"F18.imprint","IMPRINT",FACE,{"disambiguationData":[TD([[makeQuery(id+"F18.imprint","IMPRINT",EDGE,{"derivedFrom":sQuery(id+"F18.wireOp",EDGE,"E131")}),1.0]])]});
            var Q2;
            Q2=makeQuery(id+"F18.imprint","IMPRINT",FACE,{"disambiguationData":[TD([[makeQuery(id+"F18.imprint","IMPRINT",EDGE,{"derivedFrom":sQuery(id+"F18.wireOp",EDGE,"E133")}),1.0]])]});
            var Q3;
            Q3=makeQuery(id+"F18.imprint","IMPRINT",FACE,{"disambiguationData":[TD([[makeQuery(id+"F18.imprint","IMPRINT",EDGE,{"derivedFrom":sQuery(id+"F18.wireOp",EDGE,"E135.MirrorC")}),-1.0]])]});
            var Q4;
            Q4=makeQuery(id+"F18.imprint","IMPRINT",FACE,{"disambiguationData":[TD([[makeQuery(id+"F18.imprint","IMPRINT",EDGE,{"derivedFrom":sQuery(id+"F18.wireOp",EDGE,"E138.MirrorC")}),-1.0]])]});
            var Q5;
            Q5=makeQuery(id+"F18.imprint","IMPRINT",FACE,{"disambiguationData":[TD([[makeQuery(id+"F18.imprint","IMPRINT",EDGE,{"derivedFrom":sQuery(id+"F18.wireOp",EDGE,"E140.MirrorC")}),-1.0]])]});
            extrude(context, id + "F23", {"entities" : qUnion([Q0, Q1, Q2, Q3, Q4, Q5]), "operationType" : NewBodyOperationType.REMOVE, "oppositeDirection" : true, "depth" : 25 * mm});
        }
        {
            var Q0;
            Q0=makeQuery(id+"F22.boolean.opBoolean","COPY",FACE,{"derivedFrom":makeQuery(id+"F22.opExtrude","SWEPT_FACE",FACE,{"disambiguationData":[OSD([sQuery(id+"F20.wireOp",EDGE,"E149")])]})});
            var sketch = newSketch(context, id + "F24", { "sketchPlane" : qUnion([Q0])});
            skCircle(sketch, "E158", {"center": v(-75.95, -7.75) * mm, "radius": 3.1 * mm});
            skCircle(sketch, "E159", {"center": v(-67.95, -7.75) * mm, "radius": 3.1 * mm});
            skCircle(sketch, "E160", {"center": v(-60, -7.75) * mm, "radius": 3.1 * mm});
            skCircle(sketch, "E161.MirrorC", {"center": v(-28, -7.75) * mm, "radius": 3.1 * mm});
            skCircle(sketch, "E162.MirrorC", {"center": v(-20.05, -7.75) * mm, "radius": 3.1 * mm});
            skCircle(sketch, "E163.MirrorC", {"center": v(-12.05, -7.75) * mm, "radius": 3.1 * mm});
            skSolve(sketch);
        }
        {
            var Q0;
            Q0=makeQuery(id+"F24.imprint","IMPRINT",FACE,{"disambiguationData":[TD([[makeQuery(id+"F24.imprint","IMPRINT",EDGE,{"derivedFrom":sQuery(id+"F24.wireOp",EDGE,"E158")}),1.0]])]});
            var Q1;
            Q1=makeQuery(id+"F24.imprint","IMPRINT",FACE,{"disambiguationData":[TD([[makeQuery(id+"F24.imprint","IMPRINT",EDGE,{"derivedFrom":sQuery(id+"F24.wireOp",EDGE,"E159")}),1.0]])]});
            var Q2;
            Q2=makeQuery(id+"F24.imprint","IMPRINT",FACE,{"disambiguationData":[TD([[makeQuery(id+"F24.imprint","IMPRINT",EDGE,{"derivedFrom":sQuery(id+"F24.wireOp",EDGE,"E160")}),1.0]])]});
            var Q3;
            Q3=makeQuery(id+"F24.imprint","IMPRINT",FACE,{"disambiguationData":[TD([[makeQuery(id+"F24.imprint","IMPRINT",EDGE,{"derivedFrom":sQuery(id+"F24.wireOp",EDGE,"E161.MirrorC")}),-1.0]])]});
            var Q4;
            Q4=makeQuery(id+"F24.imprint","IMPRINT",FACE,{"disambiguationData":[TD([[makeQuery(id+"F24.imprint","IMPRINT",EDGE,{"derivedFrom":sQuery(id+"F24.wireOp",EDGE,"E162.MirrorC")}),-1.0]])]});
            var Q5;
            Q5=makeQuery(id+"F24.imprint","IMPRINT",FACE,{"disambiguationData":[TD([[makeQuery(id+"F24.imprint","IMPRINT",EDGE,{"derivedFrom":sQuery(id+"F24.wireOp",EDGE,"E163.MirrorC")}),-1.0]])]});
            extrude(context, id + "F25", {"entities" : qUnion([Q0, Q1, Q2, Q3, Q4, Q5]), "operationType" : NewBodyOperationType.REMOVE, "oppositeDirection" : true, "depth" : 1 * mm});
        }
        {
            var Q0;
            {var subQ0=sQuery(id+"F18.wireOp",EDGE,"E141.MirrorCS");Q0=makeQuery(id+"F18.imprint","IMPRINT",FACE,{"disambiguationData":[TD([[makeQuery(id+"F18.imprint","IMPRINT",EDGE,{"derivedFrom":subQ0}),1.0]])]});}
            var Q1;
            {var subQ0=sQuery(id+"F18.wireOp",EDGE,"E118");Q1=makeQuery(id+"F18.imprint","IMPRINT",FACE,{"disambiguationData":[TD([[makeQuery(id+"F18.imprint","IMPRINT",EDGE,{"derivedFrom":subQ0}),-1.0]])]});}
            extrude(context, id + "F26", {"entities" : qUnion([Q0, Q1]), "operationType" : NewBodyOperationType.REMOVE, "oppositeDirection" : true, "depth" : 7 * mm});
        }
        {
            var Q0;
            {var subQ0=sQuery(id+"F0.wireOp",EDGE,"E3");var subQ1=sQuery(id+"F0.wireOp",EDGE,"E2");Q0=makeQuery(id+"F26.boolean.opBoolean","SPLIT",EDGE,{"disambiguationData":[TD([makeQuery(id+"F26.opExtrude","SWEPT_FACE",FACE,{"disambiguationData":[OSD([sQuery(id+"F18.wireOp",EDGE,"E143.MirrorCS")])]})])],"derivedFrom":makeQuery(id+"F1.opExtrude","SWEPT_EDGE",EDGE,{"disambiguationData":[OSD([subQ1,subQ0])]})});}
            var Q1;
            {var subQ0=sQuery(id+"F0.wireOp",EDGE,"E4");var subQ1=sQuery(id+"F0.wireOp",EDGE,"E3");Q1=makeQuery(id+"F26.boolean.opBoolean","SPLIT",EDGE,{"disambiguationData":[TD([makeQuery(id+"F26.opExtrude","SWEPT_FACE",FACE,{"disambiguationData":[OSD([sQuery(id+"F18.wireOp",EDGE,"E143.MirrorCS")])]})])],"derivedFrom":makeQuery(id+"F1.opExtrude","SWEPT_EDGE",EDGE,{"disambiguationData":[OSD([subQ1,subQ0])]})});}
            var Q2;
            {var subQ0=sQuery(id+"F0.wireOp",EDGE,"E6");var subQ1=sQuery(id+"F0.wireOp",EDGE,"E5");Q2=makeQuery(id+"F5.boolean.opBoolean","SPLIT",EDGE,{"disambiguationData":[TD([makeQuery(id+"F5.opExtrude","SWEPT_FACE",FACE,{"disambiguationData":[OSD([sQuery(id+"F4.wireOp",EDGE,"E58.MirrorCS")])]})])],"derivedFrom":makeQuery(id+"F1.opExtrude","SWEPT_EDGE",EDGE,{"disambiguationData":[OSD([subQ1,subQ0])]})});}
            var Q3;
            {var subQ0=sQuery(id+"F0.wireOp",EDGE,"E7");var subQ1=sQuery(id+"F0.wireOp",EDGE,"E6");Q3=makeQuery(id+"F5.boolean.opBoolean","SPLIT",EDGE,{"disambiguationData":[TD([makeQuery(id+"F5.opExtrude","SWEPT_FACE",FACE,{"disambiguationData":[OSD([sQuery(id+"F4.wireOp",EDGE,"E58.MirrorCS")])]})])],"derivedFrom":makeQuery(id+"F1.opExtrude","SWEPT_EDGE",EDGE,{"disambiguationData":[OSD([subQ1,subQ0])]})});}
            var Q4;
            Q4=makeQuery(id+"F5.boolean.opBoolean","COPY",EDGE,{"derivedFrom":makeQuery(id+"F5.opExtrude","SWEPT_EDGE",EDGE,{"disambiguationData":[OSD([sQuery(id+"F0.wireOp",EDGE,"E5"),sQuery(id+"F0.wireOp",EDGE,"E6"),sQuery(id+"F4.wireOp",EDGE,"E48.MirrorCS"),sQuery(id+"F4.wireOp",EDGE,"E57.MirrorCS")])]})});
            var Q5;
            Q5=makeQuery(id+"F26.boolean.opBoolean","MERGE",EDGE,{"derivedFrom":[makeQuery(id+"F21.opExtrude","CAP_EDGE",EDGE,{"disambiguationData":[OSD([sQuery(id+"F20.wireOp",EDGE,"E156.MirrorCS"),sQuery(id+"F20.wireOp",EDGE,"E157.MirrorCS")])],"isStart":true}),makeQuery(id+"F26.opExtrude","SWEPT_EDGE",EDGE,{"disambiguationData":[OSD([sQuery(id+"F0.wireOp",EDGE,"E2"),sQuery(id+"F0.wireOp",EDGE,"E3"),sQuery(id+"F18.wireOp",EDGE,"E141.MirrorCS")])]})]});
            var Q6;
            Q6=makeQuery(id+"F26.boolean.opBoolean","COPY",EDGE,{"derivedFrom":makeQuery(id+"F26.opExtrude","SWEPT_EDGE",EDGE,{"disambiguationData":[OSD([sQuery(id+"F0.wireOp",EDGE,"E3"),sQuery(id+"F0.wireOp",EDGE,"E4"),sQuery(id+"F18.wireOp",EDGE,"E141.MirrorCS")])]})});
            var Q7;
            Q7=makeQuery(id+"F26.boolean.opBoolean","MERGE",EDGE,{"derivedFrom":[makeQuery(id+"F21.opExtrude","CAP_EDGE",EDGE,{"disambiguationData":[OSD([sQuery(id+"F20.wireOp",EDGE,"E145"),sQuery(id+"F20.wireOp",EDGE,"E146")])],"isStart":true}),makeQuery(id+"F26.opExtrude","SWEPT_EDGE",EDGE,{"disambiguationData":[OSD([sQuery(id+"F0.wireOp",EDGE,"E2"),sQuery(id+"F0.wireOp",EDGE,"E3"),sQuery(id+"F18.wireOp",EDGE,"E118"),sQuery(id+"F18.wireOp",EDGE,"E121")])]})]});
            var Q8;
            Q8=makeQuery(id+"F26.boolean.opBoolean","COPY",EDGE,{"derivedFrom":makeQuery(id+"F26.opExtrude","SWEPT_EDGE",EDGE,{"disambiguationData":[OSD([sQuery(id+"F0.wireOp",EDGE,"E3"),sQuery(id+"F0.wireOp",EDGE,"E4"),sQuery(id+"F18.wireOp",EDGE,"E118"),sQuery(id+"F18.wireOp",EDGE,"E119")])]})});
            var Q9;
            {var subQ0=sQuery(id+"F0.wireOp",EDGE,"E6");var subQ1=sQuery(id+"F0.wireOp",EDGE,"E5");Q9=makeQuery(id+"F5.boolean.opBoolean","SPLIT",EDGE,{"disambiguationData":[TD([makeQuery(id+"F5.opExtrude","SWEPT_FACE",FACE,{"disambiguationData":[OSD([sQuery(id+"F4.wireOp",EDGE,"E54")])]})])],"derivedFrom":makeQuery(id+"F1.opExtrude","SWEPT_EDGE",EDGE,{"disambiguationData":[OSD([subQ1,subQ0])]})});}
            var Q10;
            {var subQ0=sQuery(id+"F0.wireOp",EDGE,"E7");var subQ1=sQuery(id+"F0.wireOp",EDGE,"E6");Q10=makeQuery(id+"F5.boolean.opBoolean","SPLIT",EDGE,{"disambiguationData":[TD([makeQuery(id+"F5.opExtrude","SWEPT_FACE",FACE,{"disambiguationData":[OSD([sQuery(id+"F4.wireOp",EDGE,"E54")])]})])],"derivedFrom":makeQuery(id+"F1.opExtrude","SWEPT_EDGE",EDGE,{"disambiguationData":[OSD([subQ1,subQ0])]})});}
            var Q11;
            Q11=makeQuery(id+"F5.boolean.opBoolean","COPY",EDGE,{"derivedFrom":makeQuery(id+"F5.opExtrude","SWEPT_EDGE",EDGE,{"disambiguationData":[OSD([sQuery(id+"F0.wireOp",EDGE,"E5"),sQuery(id+"F0.wireOp",EDGE,"E6"),sQuery(id+"F4.wireOp",EDGE,"E55"),sQuery(id+"F4.wireOp",EDGE,"E56")])]})});
            var Q12;
            {var subQ0=sQuery(id+"F0.wireOp",EDGE,"E4");var subQ1=sQuery(id+"F0.wireOp",EDGE,"E3");Q12=makeQuery(id+"F26.boolean.opBoolean","SPLIT",EDGE,{"disambiguationData":[TD([makeQuery(id+"F26.opExtrude","SWEPT_FACE",FACE,{"disambiguationData":[OSD([sQuery(id+"F18.wireOp",EDGE,"E120")])]})])],"derivedFrom":makeQuery(id+"F1.opExtrude","SWEPT_EDGE",EDGE,{"disambiguationData":[OSD([subQ1,subQ0])]})});}
            var Q13;
            {var subQ1=sQuery(id+"F0.wireOp",EDGE,"E2");var subQ2=sQuery(id+"F0.wireOp",EDGE,"E3");Q13=makeQuery(id+"F26.boolean.opBoolean","SPLIT",EDGE,{"disambiguationData":[TD([makeQuery(id+"F26.opExtrude","SWEPT_FACE",FACE,{"disambiguationData":[OSD([sQuery(id+"F18.wireOp",EDGE,"E120")])]})])],"derivedFrom":makeQuery(id+"F1.opExtrude","SWEPT_EDGE",EDGE,{"disambiguationData":[OSD([subQ1,subQ2])]})});}
            fillet(context, id + "F27", {"entities" : qUnion([Q0, Q1, Q2, Q3, Q4, Q5, Q6, Q7, Q8, Q9, Q10, Q11, Q12, Q13]), "radius" : (7.8 / 2) * mm, "tangentPropagation" : true, "allowEdgeOverflow" : false});
        }
        {
            var Q0;
            Q0=makeQuery(id+"F5.boolean.opBoolean","COPY",EDGE,{"derivedFrom":makeQuery(id+"F5.opExtrude","SWEPT_EDGE",EDGE,{"disambiguationData":[OSD([sQuery(id+"F0.wireOp",EDGE,"E6"),sQuery(id+"F0.wireOp",EDGE,"E7"),sQuery(id+"F4.wireOp",EDGE,"E47.MirrorCS"),sQuery(id+"F4.wireOp",EDGE,"E57.MirrorCS")])]})});
            var Q1;
            Q1=makeQuery(id+"F5.boolean.opBoolean","COPY",EDGE,{"derivedFrom":makeQuery(id+"F5.opExtrude","SWEPT_EDGE",EDGE,{"disambiguationData":[OSD([sQuery(id+"F0.wireOp",EDGE,"E6"),sQuery(id+"F0.wireOp",EDGE,"E7"),sQuery(id+"F4.wireOp",EDGE,"E56")])]})});
            var Q2;
            Q2=makeQuery(id+"F21.opExtrude","CAP_EDGE",EDGE,{"disambiguationData":[OSD([sQuery(id+"F20.wireOp",EDGE,"E152.MirrorCS"),sQuery(id+"F20.wireOp",EDGE,"E154.MirrorCS")])],"isStart":true});
            var Q3;
            Q3=makeQuery(id+"F21.opExtrude","CAP_EDGE",EDGE,{"disambiguationData":[OSD([sQuery(id+"F20.wireOp",EDGE,"E148"),sQuery(id+"F20.wireOp",EDGE,"E150")])],"isStart":true});
            fillet(context, id + "F28", {"entities" : qUnion([Q0, Q1, Q2, Q3]), "radius" : 3.9 * mm, "tangentPropagation" : true, "allowEdgeOverflow" : false});
        }
    });
